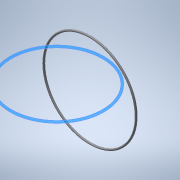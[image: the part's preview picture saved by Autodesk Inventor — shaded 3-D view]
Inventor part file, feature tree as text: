
AUTODESK INVENTOR PART (.ipt)
format: ipt  version: 2020.2 (Build 242310000, 310)  size: 123,904 bytes
history: native  units: mm
features: revolve x1, sketch x1
ambient origin geometry x8: Origin, YZ Plane, XZ Plane, XY Plane, X Axis, Y Axis, Z Axis, Center Point
bodies: Volumenkörper1 (feature_tree)
feature tree (2):
  revolve  "Umdrehung1"
  sketch  "Skizze1"  dims[d2=90.0deg d3=24.0mm]
